# Revit family: Холодильные шкафы со стеклянными дверьми POLAIR Professionale
name_source: partatom
category: Оборудование
units: mm (PartAtom-declared; Revit-internal decimal feet)

## family parameters
Всегда вертикально = Да
Классификация = Нет
На основе рабочей плоскости = Нет
Общий = Нет
При загрузке вырезать с полостями = Нет
Размер круглого соединителя = Использовать диаметр
Тип детали = Нормальный
Точка расчета площади = Нет

## types (4) — shared parameters
1 дверь S = Да
Допустимая нагрузка на полку, кг = 60
Клапан Шредера = +
Корпус = Да
Подсветка = вертикальная
Расположение агрегата = нижнее
Система электропитания В/Гц = 230/50
Терморегулятор = механический термостат или эл.  блок
Тип оттайки = автомат. с системой исп. конденсата
Тип охлаждения = динамический
Хладагент = R134a или R290
Холодильный шкаф = <По категории>
Шаг установки полок, мм = 12,5
zero-valued in all types: Отметка по умолчанию

## per-type parameters (varying)
| type | 2 Корпус | 2 дверь S | Вес брутто, кг | Вес нетто, кг | Вместимость бутылок 0,5 л, шт | Высота | Габаритные размеры, мм | Глубина | Диап. рабочих температур | Кол-во бутылок 0,5 л по глубине 1 полки, шт | Кол-во бутылок 0,5 л по ширине 1 полки, шт | Объем, л. | Потребляемая мощность, Вт, не более | Размер полки, мм | Размеры в упаковке, мм | Расход электроэнергии за сутки, кВт/ч | Условия окр. среды (темп./вл-сть,%) | Ширина |
| BC105 | Нет | Нет | 140 | 120 | 280 | 2070 мм | 697х657х2070 | 657 мм | 0....+6.5 | 7 | 8 | 500 | 500 | 595*455 | 790х744х2186 | 5 | от -30 до +40/до 80 | 697 мм |
| BC112Sd | Да | Да | 250 | 220 | 720 | 2060 мм | 1405х709х2060 | 709 мм | 0....+6,5 | 8 | 18 | 1200 | 850 | 645*536 | 1490х826х2186 | 7 | от +30 до +40/до 80 | 1405 мм |
| BC110Sd | Да | Да | 240 | 210 | 630 | 2060 мм | 1405х627х2060 | 627 мм | 0....+6,5 | 7 | 18 | 1000 | 850 | 645*455 | 1490х744х2186 | 6.5 | от +30 до +40/до 80 | 1405 мм |
| BC106 | Нет | Нет | 150 | 130 | 320 | 2070 мм | 697х730х2070 | 730 мм | 0....+6.5 | 8 | 8 | 600 | 500 | 595*536 | 790х826х2186 | 5 | от -30 до +40/до 80 | 697 мм |
